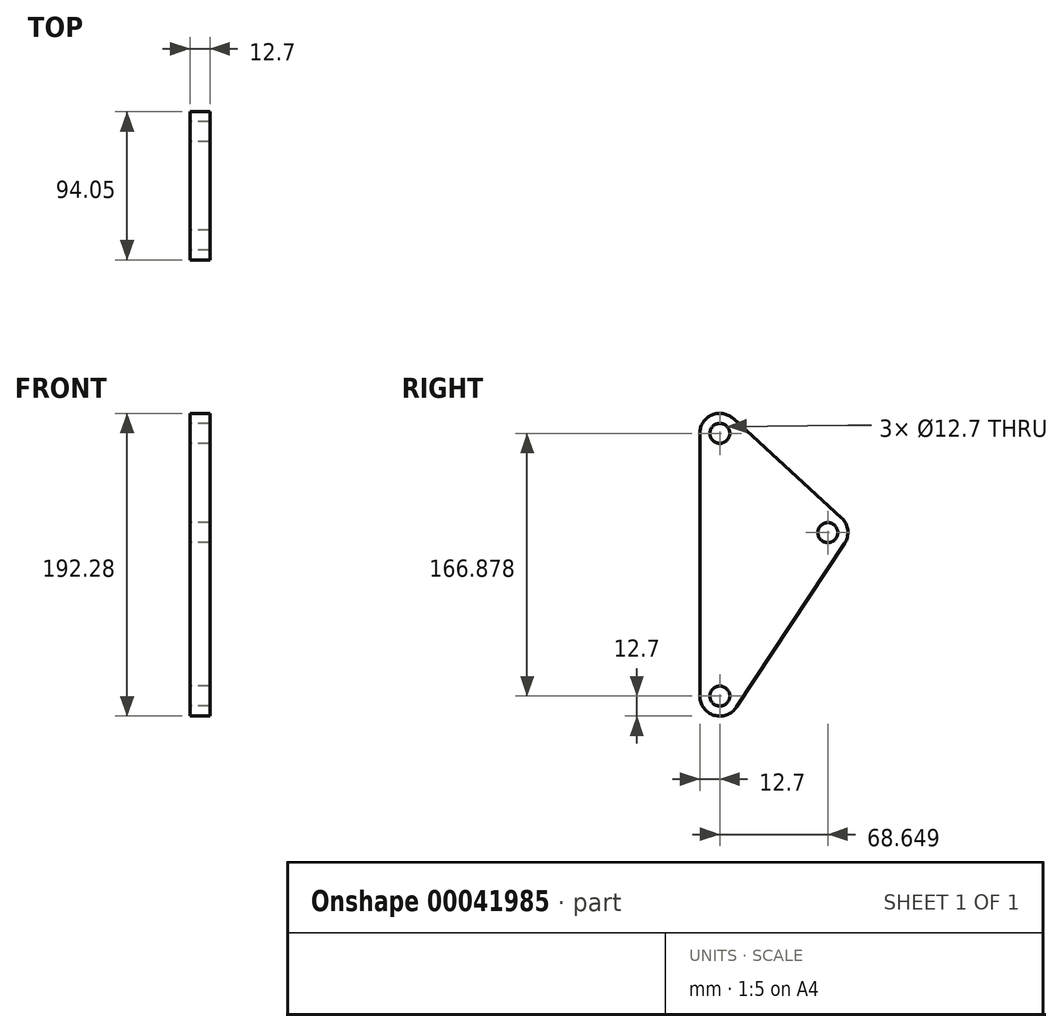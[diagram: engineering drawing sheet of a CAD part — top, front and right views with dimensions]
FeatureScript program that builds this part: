
annotation { "Feature Type Name" : "Feature", "Feature Type Description" : "" }
export const myFeature = defineFeature(function(context is Context, id is Id, definition is map)
    precondition{}
    {
        {
            var Q0;
            Q0=qCreatedBy(makeId("Right.planeOp"),FACE);
            var sketch = newSketch(context, id + "F0", { "sketchPlane" : qUnion([Q0])});
            skLineSegment(sketch, "E0", {"start": v(0, 0) * mm, "end": v(0, 166.88) * mm, "construction": true});
            skLineSegment(sketch, "E1", {"start": v(0, 166.88) * mm, "end": v(68.65, 103.82) * mm, "construction": true});
            skLineSegment(sketch, "E2", {"start": v(68.65, 103.82) * mm, "end": v(0, 0) * mm, "construction": true});
            skLineSegment(sketch, "E3.0", {"start": v(8.6, 176.23) * mm, "end": v(77.24, 113.17) * mm});
            skLineSegment(sketch, "E3.1", {"start": v(-12.7, 0) * mm, "end": v(-12.7, 166.88) * mm});
            skLineSegment(sketch, "E3.2", {"start": v(79.24, 96.81) * mm, "end": v(10.6, -7) * mm});
            skPoint(sketch, "E4.visualSharp", {"position": v(-12.7, 195.79) * mm});
            skArc(sketch, "E4.filletArc", {"start": v(8.6, 176.23) * mm, "mid": v(-5.1, 178.5) * mm, "end": v(-12.7, 166.88) * mm});
            skPoint(sketch, "E5.visualSharp", {"position": v(85.22, 105.84) * mm});
            skArc(sketch, "E5.filletArc", {"start": v(79.24, 96.81) * mm, "mid": v(81.25, 105.36) * mm, "end": v(77.24, 113.17) * mm});
            skPoint(sketch, "E6.visualSharp", {"position": v(-12.7, -42.23) * mm});
            skArc(sketch, "E6.filletArc", {"start": v(-12.7, 0) * mm, "mid": v(-3.66, -12.16) * mm, "end": v(10.6, -7) * mm});
            skCircle(sketch, "E7", {"center": v(0, 166.88) * mm, "radius": 6.35 * mm});
            skCircle(sketch, "E8", {"center": v(68.65, 103.82) * mm, "radius": 6.35 * mm});
            skCircle(sketch, "E9", {"center": v(0, 0) * mm, "radius": 6.35 * mm});
            skSolve(sketch);
        }
        {
            var Q0;
            Q0=makeQuery(id+"F0.imprint","IMPRINT",FACE,{"disambiguationData":[TD([[makeQuery(id+"F0.imprint","IMPRINT",EDGE,{"derivedFrom":sQuery(id+"F0.wireOp",EDGE,"E3.0")}),-1.0]])]});
            extrude(context, id + "F1", {"entities" : qUnion([Q0]), "depth" : 12.7 * mm});
        }
    });
